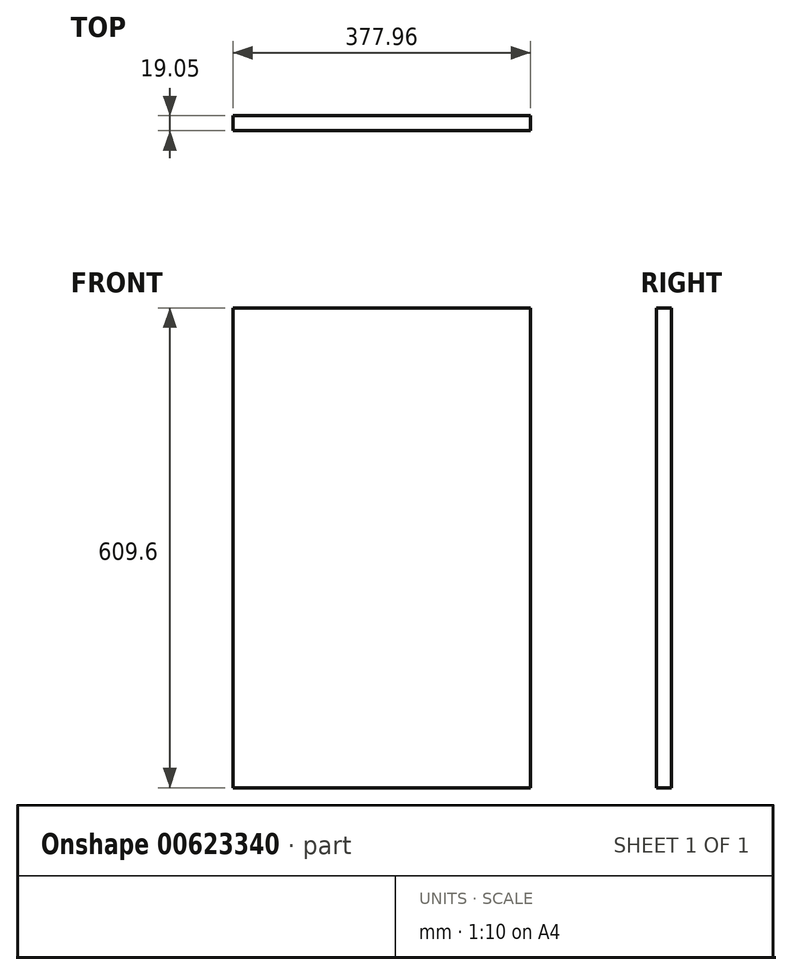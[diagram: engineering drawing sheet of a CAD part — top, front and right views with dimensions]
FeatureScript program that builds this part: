
annotation { "Feature Type Name" : "Feature", "Feature Type Description" : "" }
export const myFeature = defineFeature(function(context is Context, id is Id, definition is map)
    precondition{}
    {
        {
            var Q0;
            Q0=qCreatedBy(makeId("Front.planeOp"),FACE);
            var sketch = newSketch(context, id + "F0", { "sketchPlane" : qUnion([Q0])});
            skLineSegment(sketch, "E0.bottom", {"start": v(-188.98, 304.8) * mm, "end": v(188.98, 304.8) * mm});
            skLineSegment(sketch, "E0.top", {"start": v(-188.98, -304.8) * mm, "end": v(188.98, -304.8) * mm});
            skLineSegment(sketch, "E0.left", {"start": v(-188.98, 304.8) * mm, "end": v(-188.98, -304.8) * mm});
            skLineSegment(sketch, "E0.right", {"start": v(188.98, 304.8) * mm, "end": v(188.98, -304.8) * mm});
            skPoint(sketch, "E0.middle", {"position": v(0, 0) * mm});
            skSolve(sketch);
        }
        {
            var Q0;
            Q0=makeQuery(id+"F0.imprint","IMPRINT",FACE,{"disambiguationData":[TD([[makeQuery(id+"F0.imprint","IMPRINT",EDGE,{"derivedFrom":sQuery(id+"F0.wireOp",EDGE,"E0.bottom")}),-1.0]])]});
            extrude(context, id + "F1", {"entities" : qUnion([Q0]), "depth" : 19.05 * mm, "offsetDistance" : 25.4 * mm});
        }
    });
